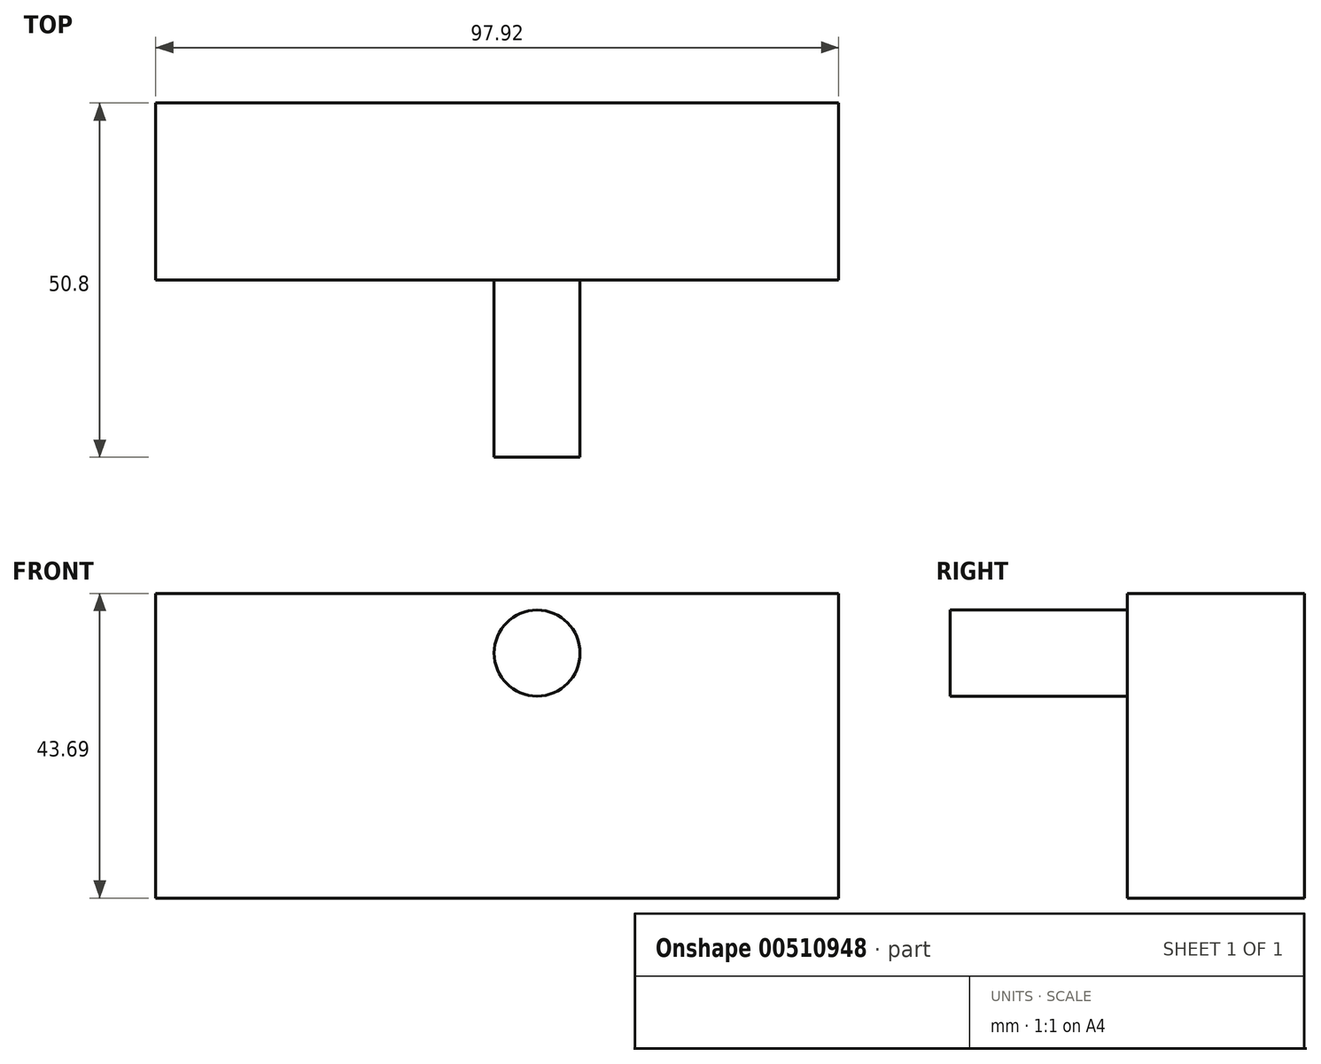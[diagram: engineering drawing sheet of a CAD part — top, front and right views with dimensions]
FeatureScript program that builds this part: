
annotation { "Feature Type Name" : "Feature", "Feature Type Description" : "" }
export const myFeature = defineFeature(function(context is Context, id is Id, definition is map)
    precondition{}
    {
        {
            var Q0;
            Q0=qCreatedBy(makeId("Front.planeOp"),FACE);
            var sketch = newSketch(context, id + "F0", { "sketchPlane" : qUnion([Q0])});
            skLineSegment(sketch, "E0.bottom", {"start": v(-23.54, 13) * mm, "end": v(74.38, 13) * mm});
            skLineSegment(sketch, "E0.top", {"start": v(-23.54, 56.69) * mm, "end": v(74.38, 56.69) * mm});
            skLineSegment(sketch, "E0.left", {"start": v(-23.54, 13) * mm, "end": v(-23.54, 56.69) * mm});
            skLineSegment(sketch, "E0.right", {"start": v(74.38, 13) * mm, "end": v(74.38, 56.69) * mm});
            skSolve(sketch);
        }
        {
            var Q0;
            Q0 = qSketchRegion(id + "F0", true);
            extrude(context, id + "F1", {"entities" : qUnion([Q0]), "depth" : 25.4 * mm});
        }
        {
            var Q0;
            Q0=makeQuery(id+"F1.opExtrude","CAP_FACE",FACE,{"disambiguationData":[OSD([sQuery(id+"F0.wireOp",EDGE,"E0.bottom"),sQuery(id+"F0.wireOp",EDGE,"E0.top"),sQuery(id+"F0.wireOp",EDGE,"E0.left"),sQuery(id+"F0.wireOp",EDGE,"E0.right")])],"isStart":false});
            var sketch = newSketch(context, id + "F2", { "sketchPlane" : qUnion([Q0])});
            skCircle(sketch, "E1", {"center": v(31.13, 48.12) * mm, "radius": 6.17 * mm});
            skSolve(sketch);
        }
        {
            var Q0;
            Q0=makeQuery(id+"F2.imprint","IMPRINT",FACE,{"disambiguationData":[TD([[makeQuery(id+"F2.imprint","IMPRINT",EDGE,{"derivedFrom":sQuery(id+"F2.wireOp",EDGE,"E1")}),1.0]])]});
            var Q1;
            Q1 = qSketchRegion(id + "F2", true);
            extrude(context, id + "F3", {"entities" : qUnion([Q0, Q1]), "operationType" : NewBodyOperationType.ADD, "depth" : 25.4 * mm});
        }
    });
